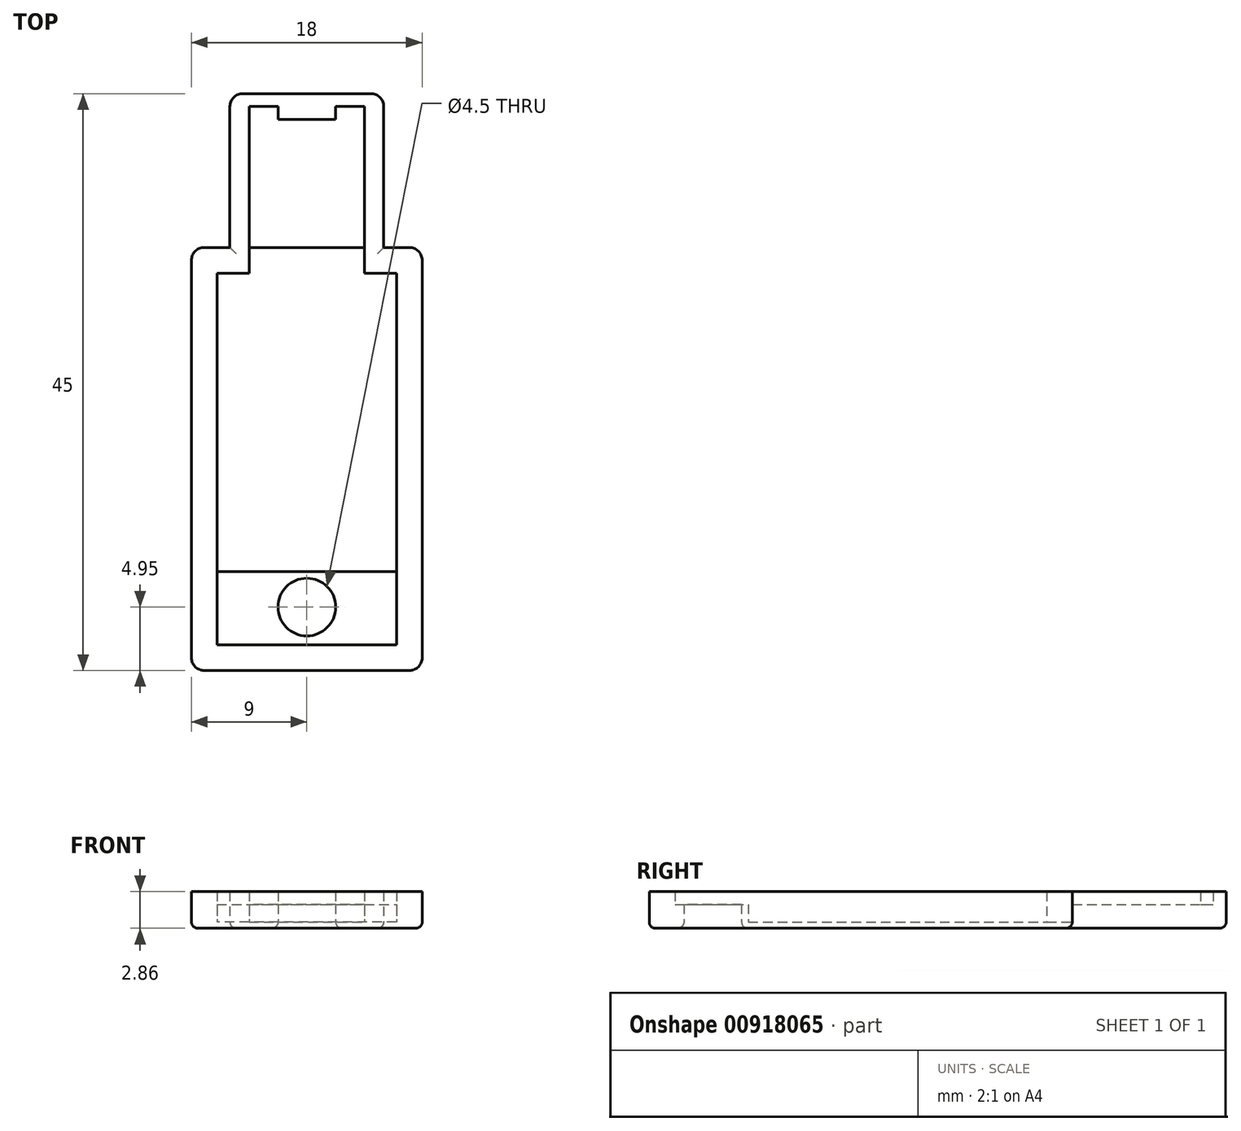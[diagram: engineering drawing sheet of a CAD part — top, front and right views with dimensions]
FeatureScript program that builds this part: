
annotation { "Feature Type Name" : "Feature", "Feature Type Description" : "" }
export const myFeature = defineFeature(function(context is Context, id is Id, definition is map)
    precondition{}
    {
        {
            var Q0;
            Q0=qCreatedBy(makeId("Top.planeOp"),FACE);
            var sketch = newSketch(context, id + "F0", { "sketchPlane" : qUnion([Q0])});
            skLineSegment(sketch, "E0", {"start": v(0, 0) * mm, "end": v(14, 0) * mm});
            skLineSegment(sketch, "E1", {"start": v(14, 0) * mm, "end": v(14, 29) * mm});
            skLineSegment(sketch, "E2", {"start": v(14, 29) * mm, "end": v(11.5, 29) * mm});
            skLineSegment(sketch, "E3", {"start": v(11.5, 29) * mm, "end": v(11.5, 42) * mm});
            skLineSegment(sketch, "E4", {"start": v(2.5, 42) * mm, "end": v(2.5, 29) * mm});
            skLineSegment(sketch, "E5", {"start": v(2.5, 29) * mm, "end": v(0, 29) * mm});
            skLineSegment(sketch, "E6", {"start": v(0, 29) * mm, "end": v(0, 0) * mm});
            skLineSegment(sketch, "E7", {"start": v(11.5, 42) * mm, "end": v(9.25, 42) * mm});
            skLineSegment(sketch, "E8", {"start": v(9.25, 42) * mm, "end": v(9.25, 41) * mm});
            skLineSegment(sketch, "E9", {"start": v(9.25, 41) * mm, "end": v(4.75, 41) * mm});
            skLineSegment(sketch, "E10", {"start": v(4.75, 41) * mm, "end": v(4.75, 42) * mm});
            skLineSegment(sketch, "E11", {"start": v(4.75, 42) * mm, "end": v(2.5, 42) * mm});
            skLineSegment(sketch, "E12", {"start": v(-1, -2) * mm, "end": v(15, -2) * mm});
            skLineSegment(sketch, "E13", {"start": v(16, -1) * mm, "end": v(16, 30) * mm});
            skLineSegment(sketch, "E14", {"start": v(15, 31) * mm, "end": v(13, 31) * mm});
            skLineSegment(sketch, "E15", {"start": v(13, 31) * mm, "end": v(13, 42) * mm});
            skLineSegment(sketch, "E16", {"start": v(12, 43) * mm, "end": v(2, 43) * mm});
            skLineSegment(sketch, "E17", {"start": v(-1, 31) * mm, "end": v(-1, 31) * mm});
            skLineSegment(sketch, "E18", {"start": v(-2, 30) * mm, "end": v(-2, -1) * mm});
            skPoint(sketch, "E19.visualSharp", {"position": v(13, 43) * mm});
            skArc(sketch, "E19.filletArc", {"start": v(13, 42) * mm, "mid": v(12.7, 42.7) * mm, "end": v(12, 43) * mm});
            skPoint(sketch, "E20.visualSharp", {"position": v(-2, 31) * mm});
            skArc(sketch, "E20.filletArc", {"start": v(-1, 31) * mm, "mid": v(-1.7, 30.7) * mm, "end": v(-2, 30) * mm});
            skPoint(sketch, "E21.visualSharp", {"position": v(13, 31) * mm});
            skPoint(sketch, "E22.visualSharp", {"position": v(16, 31) * mm});
            skArc(sketch, "E22.filletArc", {"start": v(16, 30) * mm, "mid": v(15.7, 30.7) * mm, "end": v(15, 31) * mm});
            skPoint(sketch, "E23.visualSharp", {"position": v(16, -2) * mm});
            skArc(sketch, "E23.filletArc", {"start": v(15, -2) * mm, "mid": v(15.7, -1.7) * mm, "end": v(16, -1) * mm});
            skPoint(sketch, "E24.visualSharp", {"position": v(-2, -2) * mm});
            skArc(sketch, "E24.filletArc", {"start": v(-2, -1) * mm, "mid": v(-1.7, -1.7) * mm, "end": v(-1, -2) * mm});
            skLineSegment(sketch, "E25", {"start": v(-1, 31) * mm, "end": v(1, 31) * mm});
            skLineSegment(sketch, "E26", {"start": v(1, 42) * mm, "end": v(1, 31) * mm});
            skPoint(sketch, "E27.visualSharp", {"position": v(1, 43) * mm});
            skArc(sketch, "E27.filletArc", {"start": v(2, 43) * mm, "mid": v(1.3, 42.7) * mm, "end": v(1, 42) * mm});
            skPoint(sketch, "E28.visualSharp", {"position": v(1, 31) * mm});
            skCircle(sketch, "E29", {"center": v(7, 18.8) * mm, "radius": 4.5 * mm});
            skCircle(sketch, "E30", {"center": v(7, 2.95) * mm, "radius": 2.25 * mm});
            skLineSegment(sketch, "E31", {"start": v(7, 41) * mm, "end": v(7, 0) * mm, "construction": true});
            skLineSegment(sketch, "E32", {"start": v(1, 31) * mm, "end": v(2.5, 31) * mm, "construction": true});
            skLineSegment(sketch, "E33", {"start": v(13, 31) * mm, "end": v(11.5, 31) * mm, "construction": true});
            skLineSegment(sketch, "E34", {"start": v(2.5, 31) * mm, "end": v(11.5, 31) * mm});
            skLineSegment(sketch, "E35", {"start": v(14, 5.72) * mm, "end": v(0, 5.72) * mm});
            skSolve(sketch);
        }
        {
            var Q0;
            Q0=makeQuery(id+"F0.imprint","IMPRINT",FACE,{"disambiguationData":[TD([[makeQuery(id+"F0.imprint","IMPRINT",EDGE,{"derivedFrom":sQuery(id+"F0.wireOp",EDGE,"E0")}),-1.0]])]});
            extrude(context, id + "F1", {"entities" : qUnion([Q0]), "depth" : 2.36 * mm, "offsetDistance" : 25 * mm});
        }
        {
            var Q0;
            Q0=makeQuery(id+"F0.imprint","IMPRINT",FACE,{"disambiguationData":[TD([[makeQuery(id+"F0.imprint","IMPRINT",EDGE,{"derivedFrom":sQuery(id+"F0.wireOp",EDGE,"E0")}),-1.0]])]});
            var Q1;
            Q1=makeQuery(id+"F0.imprint","IMPRINT",FACE,{"disambiguationData":[TD([[makeQuery(id+"F0.imprint","IMPRINT",EDGE,{"derivedFrom":sQuery(id+"F0.wireOp",EDGE,"E0")}),1.0]])]});
            var Q2;
            {var subQ3=sQuery(id+"F0.wireOp",EDGE,"E7");Q2=makeQuery(id+"F0.imprint","IMPRINT",FACE,{"disambiguationData":[TD([[makeQuery(id+"F0.imprint","IMPRINT",EDGE,{"derivedFrom":subQ3}),1.0]])]});}
            var Q3;
            {var subQ1=sQuery(id+"F0.wireOp",EDGE,"E2");Q3=makeQuery(id+"F0.imprint","IMPRINT",FACE,{"disambiguationData":[TD([[makeQuery(id+"F0.imprint","IMPRINT",EDGE,{"derivedFrom":subQ1}),1.0]])]});}
            var Q4;
            Q4=makeQuery(id+"F0.imprint","IMPRINT",FACE,{"disambiguationData":[TD([[makeQuery(id+"F0.imprint","IMPRINT",EDGE,{"derivedFrom":sQuery(id+"F0.wireOp",EDGE,"E29")}),1.0]])]});
            extrude(context, id + "F2", {"entities" : qUnion([Q0, Q1, Q2, Q3, Q4]), "operationType" : NewBodyOperationType.ADD, "oppositeDirection" : true, "depth" : 0.5 * mm, "offsetDistance" : 25 * mm});
        }
        {
            var Q0;
            Q0=makeQuery(id+"F2.opExtrude","CAP_FACE",FACE,{"disambiguationData":[OSD([sQuery(id+"F0.wireOp",EDGE,"E12"),sQuery(id+"F0.wireOp",EDGE,"E13"),sQuery(id+"F0.wireOp",EDGE,"E14"),sQuery(id+"F0.wireOp",EDGE,"E15"),sQuery(id+"F0.wireOp",EDGE,"E16"),sQuery(id+"F0.wireOp",EDGE,"E18"),sQuery(id+"F0.wireOp",EDGE,"E19.filletArc"),sQuery(id+"F0.wireOp",EDGE,"E20.filletArc"),sQuery(id+"F0.wireOp",EDGE,"E22.filletArc"),sQuery(id+"F0.wireOp",EDGE,"E23.filletArc"),sQuery(id+"F0.wireOp",EDGE,"E24.filletArc"),sQuery(id+"F0.wireOp",EDGE,"E25"),sQuery(id+"F0.wireOp",EDGE,"E26"),sQuery(id+"F0.wireOp",EDGE,"E27.filletArc"),sQuery(id+"F0.wireOp",EDGE,"E30")])],"isStart":false});
            fillet(context, id + "F3", {"entities" : qUnion([Q0]), "radius" : 0.5 * mm, "tangentPropagation" : true, "allowEdgeOverflow" : false});
        }
        {
            var Q0;
            {var subQ3=sQuery(id+"F0.wireOp",EDGE,"E7");Q0=makeQuery(id+"F0.imprint","IMPRINT",FACE,{"disambiguationData":[TD([[makeQuery(id+"F0.imprint","IMPRINT",EDGE,{"derivedFrom":subQ3}),1.0]])]});}
            extrude(context, id + "F4", {"entities" : qUnion([Q0]), "operationType" : NewBodyOperationType.ADD, "depth" : 1.36 * mm, "offsetDistance" : 25 * mm});
        }
        {
            var Q0;
            {var subQ1=sQuery(id+"F0.wireOp",EDGE,"E0");Q0=makeQuery(id+"F0.imprint","IMPRINT",FACE,{"disambiguationData":[TD([[makeQuery(id+"F0.imprint","IMPRINT",EDGE,{"derivedFrom":subQ1}),1.0]])]});}
            extrude(context, id + "F5", {"entities" : qUnion([Q0]), "operationType" : NewBodyOperationType.ADD, "depth" : 1.36 * mm, "offsetDistance" : 25 * mm});
        }
    });
